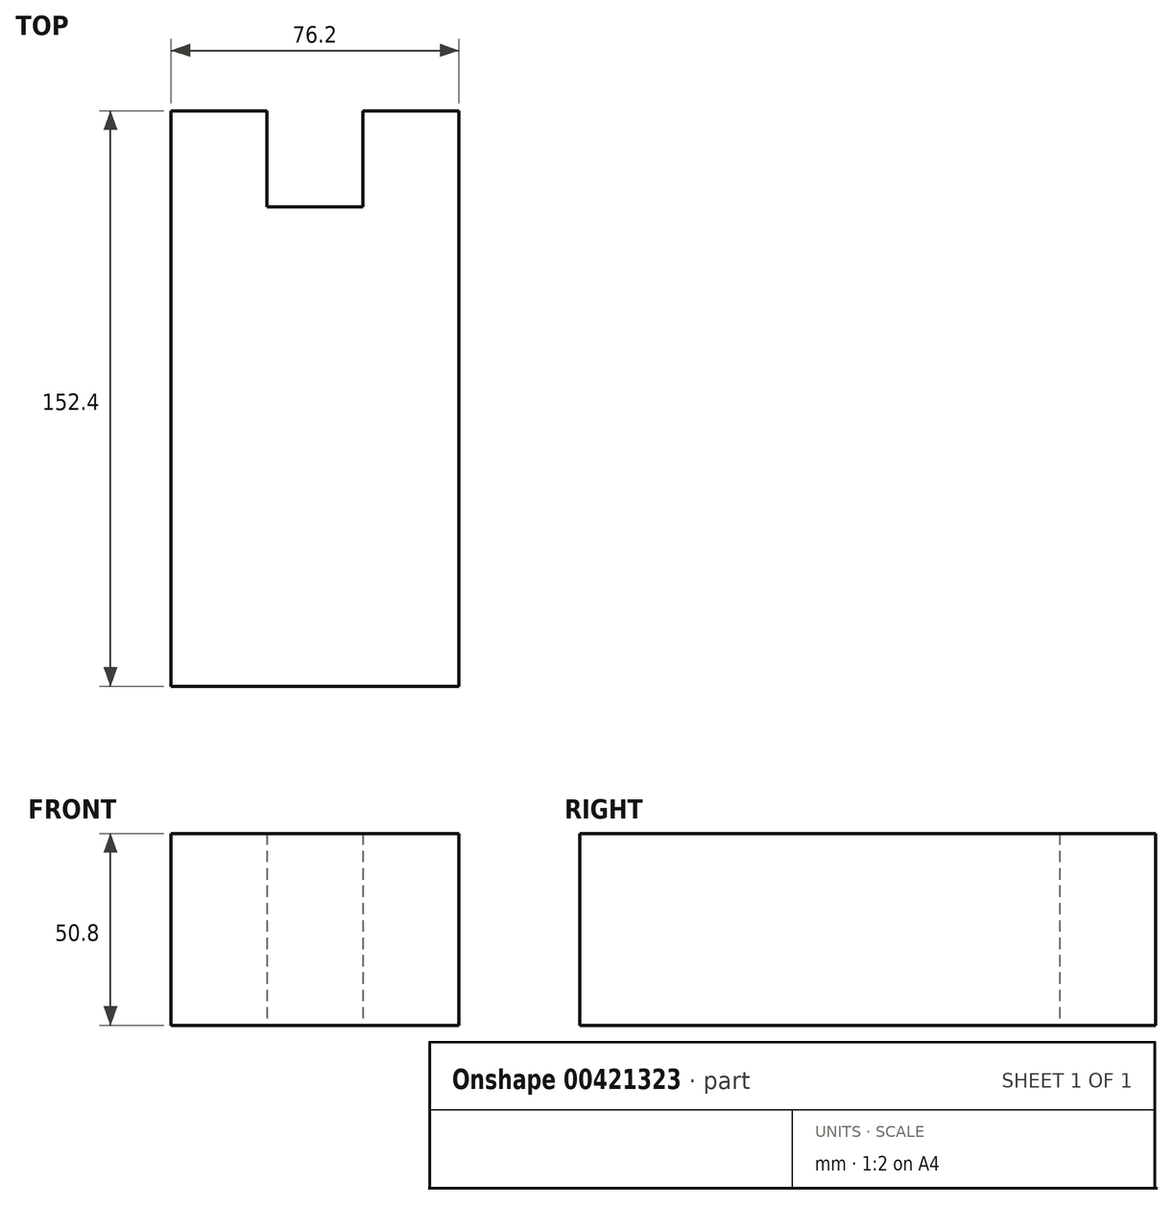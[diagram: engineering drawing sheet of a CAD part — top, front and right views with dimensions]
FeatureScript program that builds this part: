
annotation { "Feature Type Name" : "Feature", "Feature Type Description" : "" }
export const myFeature = defineFeature(function(context is Context, id is Id, definition is map)
    precondition{}
    {
        {
            var Q0;
            Q0=qCreatedBy(makeId("Top.planeOp"),FACE);
            var sketch = newSketch(context, id + "F0", { "sketchPlane" : qUnion([Q0])});
            skLineSegment(sketch, "E0", {"start": v(0, 0) * mm, "end": v(76.2, 0) * mm});
            skLineSegment(sketch, "E1", {"start": v(0, 0) * mm, "end": v(0, 152.4) * mm});
            skLineSegment(sketch, "E2", {"start": v(76.2, 0) * mm, "end": v(76.2, 152.4) * mm});
            skLineSegment(sketch, "E3", {"start": v(0, 152.4) * mm, "end": v(25.4, 152.4) * mm});
            skLineSegment(sketch, "E4", {"start": v(76.2, 152.4) * mm, "end": v(50.8, 152.4) * mm});
            skLineSegment(sketch, "E5", {"start": v(25.4, 152.4) * mm, "end": v(25.4, 127) * mm});
            skLineSegment(sketch, "E6", {"start": v(25.4, 127) * mm, "end": v(50.8, 127) * mm});
            skLineSegment(sketch, "E7", {"start": v(50.8, 152.4) * mm, "end": v(50.8, 127) * mm});
            skSolve(sketch);
        }
        {
            var Q0;
            Q0=makeQuery(id+"F0.imprint","IMPRINT",FACE,{"disambiguationData":[TD([[makeQuery(id+"F0.imprint","IMPRINT",EDGE,{"derivedFrom":sQuery(id+"F0.wireOp",EDGE,"E0")}),1.0]])]});
            extrude(context, id + "F1", {"entities" : qUnion([Q0]), "depth" : 50.8 * mm});
        }
    });
